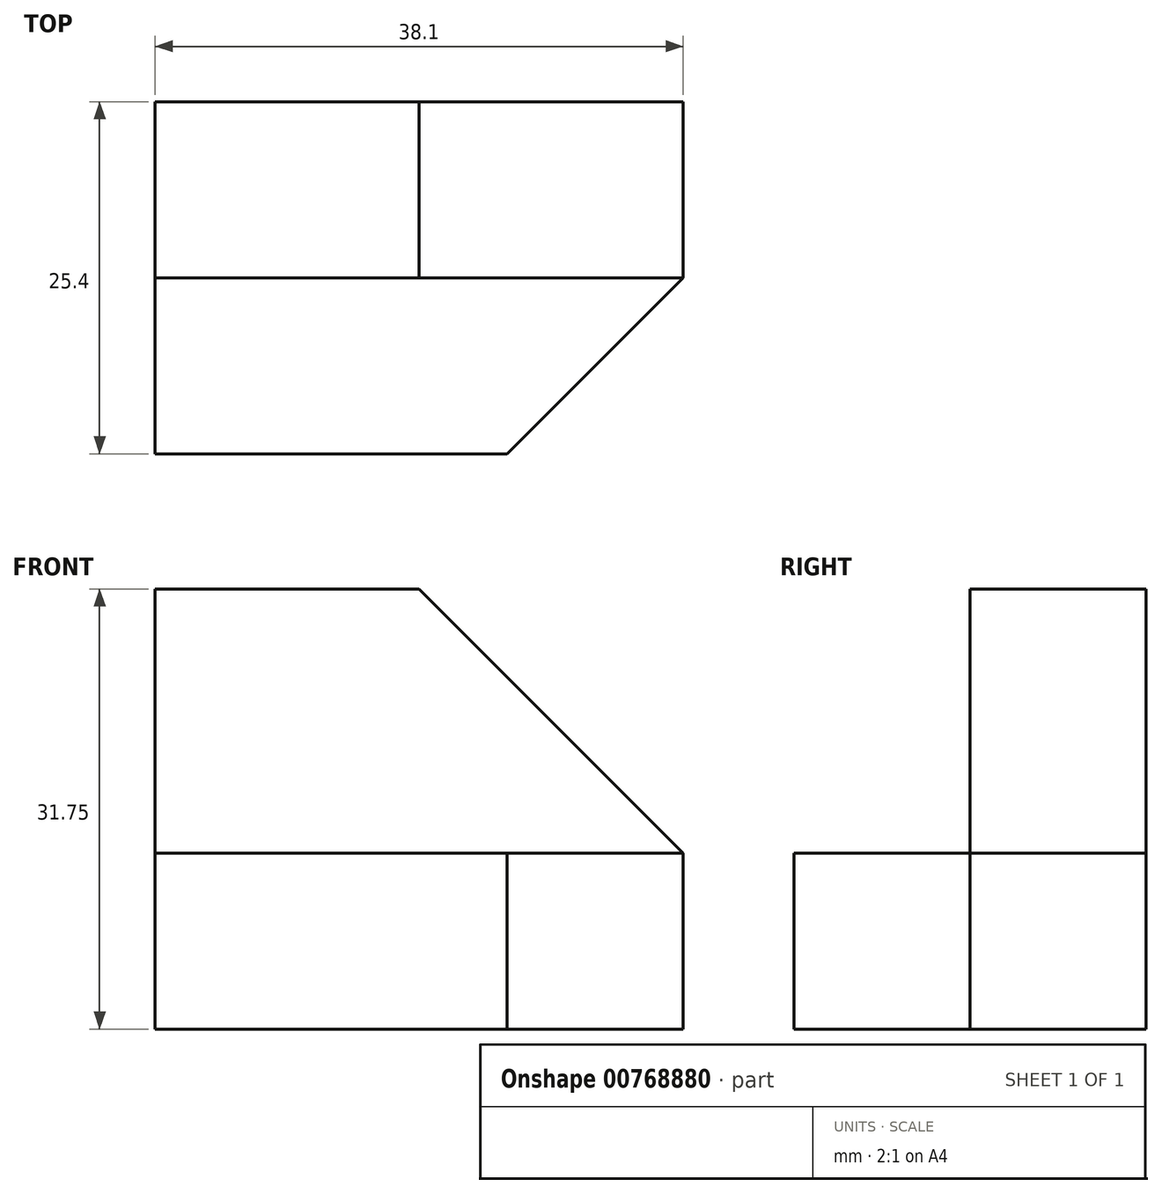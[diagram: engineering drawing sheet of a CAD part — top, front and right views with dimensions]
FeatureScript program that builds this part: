
annotation { "Feature Type Name" : "Feature", "Feature Type Description" : "" }
export const myFeature = defineFeature(function(context is Context, id is Id, definition is map)
    precondition{}
    {
        {
            var Q0;
            Q0=qCreatedBy(makeId("Front.planeOp"),FACE);
            var sketch = newSketch(context, id + "F0", { "sketchPlane" : qUnion([Q0])});
            skLineSegment(sketch, "E0", {"start": v(0, 0) * mm, "end": v(38.1, 0) * mm});
            skLineSegment(sketch, "E1", {"start": v(38.1, 0) * mm, "end": v(38.1, 31.75) * mm});
            skLineSegment(sketch, "E2", {"start": v(38.1, 31.75) * mm, "end": v(0, 31.75) * mm});
            skLineSegment(sketch, "E3", {"start": v(0, 31.75) * mm, "end": v(0, 0) * mm});
            skSolve(sketch);
        }
        {
            var Q0;
            Q0=makeQuery(id+"F0.imprint","IMPRINT",FACE,{"disambiguationData":[TD([[makeQuery(id+"F0.imprint","IMPRINT",EDGE,{"derivedFrom":sQuery(id+"F0.wireOp",EDGE,"E0")}),1.0]])]});
            extrude(context, id + "F1", {"entities" : qUnion([Q0]), "depth" : 25.4 * mm, "offsetDistance" : 25.4 * mm});
        }
        {
            var Q0;
            Q0=makeQuery(id+"F1.opExtrude","SWEPT_FACE",FACE,{"disambiguationData":[OSD([sQuery(id+"F0.wireOp",EDGE,"E2")])]});
            var sketch = newSketch(context, id + "F2", { "sketchPlane" : qUnion([Q0])});
            skLineSegment(sketch, "E4", {"start": v(0, -12.7) * mm, "end": v(38.1, -12.7) * mm});
            skSolve(sketch);
        }
        {
            var Q0;
            {var subQ0=sQuery(id+"F2.wireOp",EDGE,"E4");Q0=makeQuery(id+"F2.imprint","IMPRINT",FACE,{"disambiguationData":[TD([[makeQuery(id+"F2.imprint","IMPRINT",EDGE,{"derivedFrom":subQ0}),-1.0]])]});}
            extrude(context, id + "F3", {"entities" : qUnion([Q0]), "operationType" : NewBodyOperationType.REMOVE, "oppositeDirection" : true, "depth" : 19.05 * mm, "offsetDistance" : 25.4 * mm});
        }
        {
            var Q0;
            Q0=makeQuery(id+"F3.boolean.opBoolean","COPY",FACE,{"derivedFrom":makeQuery(id+"F3.opExtrude","CAP_FACE",FACE,{"disambiguationData":[OSD([sQuery(id+"F0.wireOp",EDGE,"E1"),sQuery(id+"F0.wireOp",EDGE,"E2"),sQuery(id+"F0.wireOp",EDGE,"E3"),sQuery(id+"F2.wireOp",EDGE,"E4")])],"isStart":false})});
            var sketch = newSketch(context, id + "F4", { "sketchPlane" : qUnion([Q0])});
            skLineSegment(sketch, "E5", {"start": v(38.1, -25.4) * mm, "end": v(25.4, -25.4) * mm});
            skLineSegment(sketch, "E6", {"start": v(25.4, -25.4) * mm, "end": v(38.1, -12.7) * mm});
            skSolve(sketch);
        }
        {
            var Q0;
            Q0=makeQuery(id+"F3.boolean.opBoolean","COPY",FACE,{"derivedFrom":makeQuery(id+"F3.opExtrude","SWEPT_FACE",FACE,{"disambiguationData":[OSD([sQuery(id+"F2.wireOp",EDGE,"E4")])]})});
            var sketch = newSketch(context, id + "F5", { "sketchPlane" : qUnion([Q0])});
            skLineSegment(sketch, "E7", {"start": v(0, 31.75) * mm, "end": v(19.05, 31.75) * mm});
            skLineSegment(sketch, "E8", {"start": v(19.05, 31.75) * mm, "end": v(38.1, 12.7) * mm});
            skSolve(sketch);
        }
        {
            var Q0;
            {var subQ0=sQuery(id+"F5.wireOp",EDGE,"E8");Q0=makeQuery(id+"F5.imprint","IMPRINT",FACE,{"disambiguationData":[TD([[makeQuery(id+"F5.imprint","IMPRINT",EDGE,{"derivedFrom":subQ0}),1.0]])]});}
            extrude(context, id + "F6", {"entities" : qUnion([Q0]), "operationType" : NewBodyOperationType.REMOVE, "oppositeDirection" : true, "depth" : 12.7 * mm, "offsetDistance" : 25.4 * mm});
        }
        {
            var Q0;
            Q0=makeQuery(id+"F4.imprint","IMPRINT",FACE,{"disambiguationData":[TD([[makeQuery(id+"F4.imprint","IMPRINT",EDGE,{"derivedFrom":sQuery(id+"F4.wireOp",EDGE,"E5")}),-1.0]])]});
            extrude(context, id + "F7", {"entities" : qUnion([Q0]), "operationType" : NewBodyOperationType.REMOVE, "oppositeDirection" : true, "depth" : 12.7 * mm, "offsetDistance" : 25.4 * mm});
        }
    });
